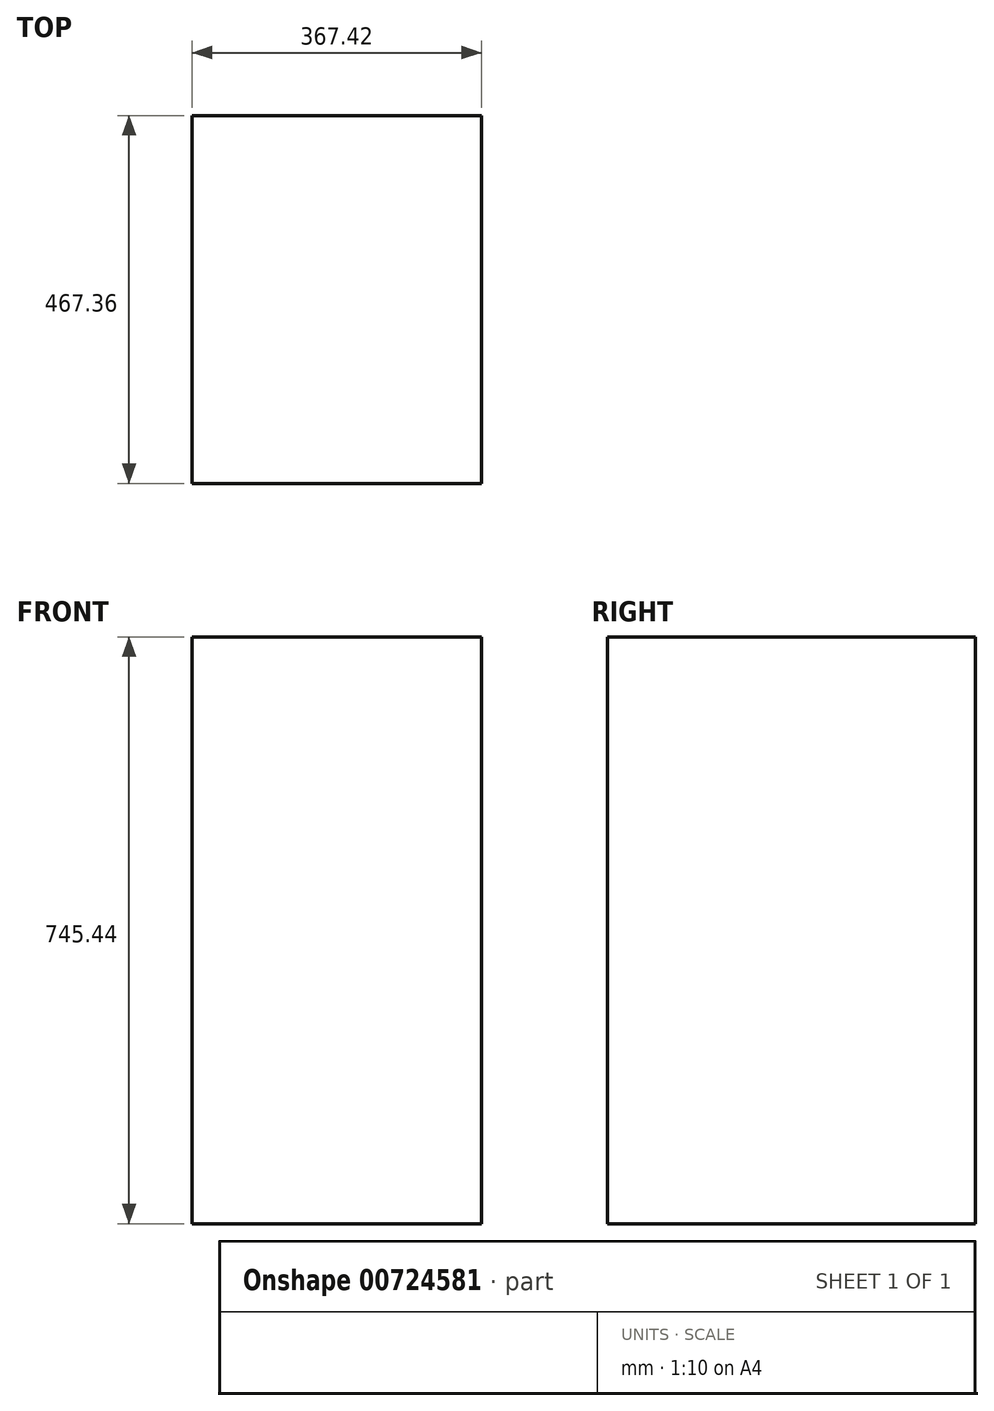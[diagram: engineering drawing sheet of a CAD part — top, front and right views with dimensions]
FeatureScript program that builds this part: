
annotation { "Feature Type Name" : "Feature", "Feature Type Description" : "" }
export const myFeature = defineFeature(function(context is Context, id is Id, definition is map)
    precondition{}
    {
        {
            var Q0;
            Q0=qCreatedBy(makeId("Front.planeOp"),FACE);
            var sketch = newSketch(context, id + "F0", { "sketchPlane" : qUnion([Q0])});
            skLineSegment(sketch, "E0.bottom", {"start": v(-166, 264.96) * mm, "end": v(201.4, 264.96) * mm});
            skLineSegment(sketch, "E0.top", {"start": v(-166, -480.48) * mm, "end": v(201.4, -480.48) * mm});
            skLineSegment(sketch, "E0.left", {"start": v(-166, 264.96) * mm, "end": v(-166, -480.48) * mm});
            skLineSegment(sketch, "E0.right", {"start": v(201.4, 264.96) * mm, "end": v(201.4, -480.48) * mm});
            skSolve(sketch);
        }
        {
            var Q0;
            Q0 = qSketchRegion(id + "F0", true);
            extrude(context, id + "F1", {"entities" : qUnion([Q0]), "depth" : 467.36 * mm, "offsetDistance" : 25.4 * mm});
        }
    });
